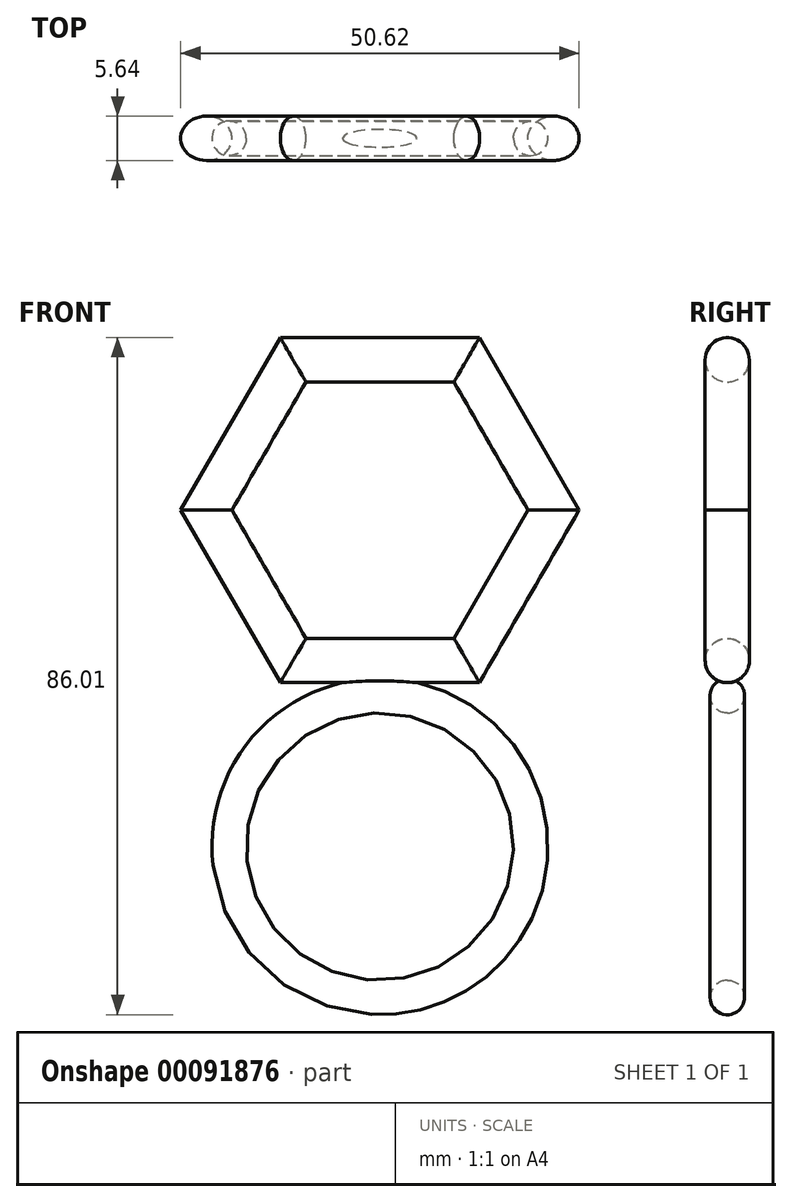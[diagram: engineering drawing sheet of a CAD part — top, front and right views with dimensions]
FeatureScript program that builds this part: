
annotation { "Feature Type Name" : "Feature", "Feature Type Description" : "" }
export const myFeature = defineFeature(function(context is Context, id is Id, definition is map)
    precondition{}
    {
        {
            var Q0;
            Q0=qCreatedBy(makeId("Front.planeOp"),FACE);
            var sketch = newSketch(context, id + "F0", { "sketchPlane" : qUnion([Q0])});
            skCircle(sketch, "E0", {"center": v(0, 0) * mm, "radius": 19.26 * mm});
            skPoint(sketch, "E1", {"position": v(0, 19.26) * mm});
            skSolve(sketch);
        }
        {
            var Q0;
            Q0=qCreatedBy(makeId("Right.planeOp"),FACE);
            var sketch = newSketch(context, id + "F1", { "sketchPlane" : qUnion([Q0])});
            skCircle(sketch, "E2", {"center": v(0, 19.16) * mm, "radius": 2.2 * mm});
            skSolve(sketch);
        }
        {
            var Q0;
            Q0=makeQuery(id+"F1.imprint","IMPRINT",FACE,{"disambiguationData":[TD([[makeQuery(id+"F1.imprint","IMPRINT",EDGE,{"derivedFrom":sQuery(id+"F1.wireOp",EDGE,"E2")}),1.0]])]});
            var Q1;
            Q1=sQuery(id+"F0.wireOp",EDGE,"E0");
            sweep(context, id + "F2", {"profiles" : qUnion([Q0]), "path" : qUnion([Q1])});
        }
        {
            var Q0;
            Q0=qCreatedBy(makeId("Front.planeOp"),FACE);
            var sketch = newSketch(context, id + "F3", { "sketchPlane" : qUnion([Q0])});
            skCircle(sketch, "E3.cCircle", {"center": v(0, 42.74) * mm, "radius": 15.03 * mm, "construction": true});
            skLineSegment(sketch, "E3.0", {"start": v(8.68, 27.71) * mm, "end": v(-8.68, 27.71) * mm});
            skLineSegment(sketch, "E3.1", {"start": v(-8.68, 27.71) * mm, "end": v(-17.35, 42.74) * mm});
            skLineSegment(sketch, "E3.2", {"start": v(-17.35, 42.74) * mm, "end": v(-8.68, 57.77) * mm});
            skLineSegment(sketch, "E3.3", {"start": v(-8.68, 57.77) * mm, "end": v(8.68, 57.77) * mm});
            skLineSegment(sketch, "E3.4", {"start": v(8.68, 57.77) * mm, "end": v(17.35, 42.74) * mm});
            skLineSegment(sketch, "E3.5", {"start": v(17.35, 42.74) * mm, "end": v(8.68, 27.71) * mm});
            skPoint(sketch, "E3.0.midPoint", {"position": v(0, 27.71) * mm});
            skSolve(sketch);
        }
        {
            var Q0;
            Q0=qCreatedBy(makeId("Right.planeOp"),FACE);
            var sketch = newSketch(context, id + "F4", { "sketchPlane" : qUnion([Q0])});
            skCircle(sketch, "E4", {"center": v(0, 61.84) * mm, "radius": 2.82 * mm});
            skSolve(sketch);
        }
        {
            var Q0;
            Q0=makeQuery(id+"F4.imprint","IMPRINT",FACE,{"disambiguationData":[TD([[makeQuery(id+"F4.imprint","IMPRINT",EDGE,{"derivedFrom":sQuery(id+"F4.wireOp",EDGE,"E4")}),1.0]])]});
            var Q1;
            Q1=sQuery(id+"F3.wireOp",EDGE,"E3.1");
            var Q2;
            Q2=sQuery(id+"F3.wireOp",EDGE,"E3.2");
            var Q3;
            Q3=sQuery(id+"F3.wireOp",EDGE,"E3.3");
            var Q4;
            Q4=sQuery(id+"F3.wireOp",EDGE,"E3.4");
            var Q5;
            Q5=sQuery(id+"F3.wireOp",EDGE,"E3.5");
            var Q6;
            Q6=sQuery(id+"F3.wireOp",EDGE,"E3.0");
            sweep(context, id + "F5", {"operationType" : NewBodyOperationType.ADD, "profiles" : qUnion([Q0]), "path" : qUnion([Q1, Q2, Q3, Q4, Q5, Q6])});
        }
    });
